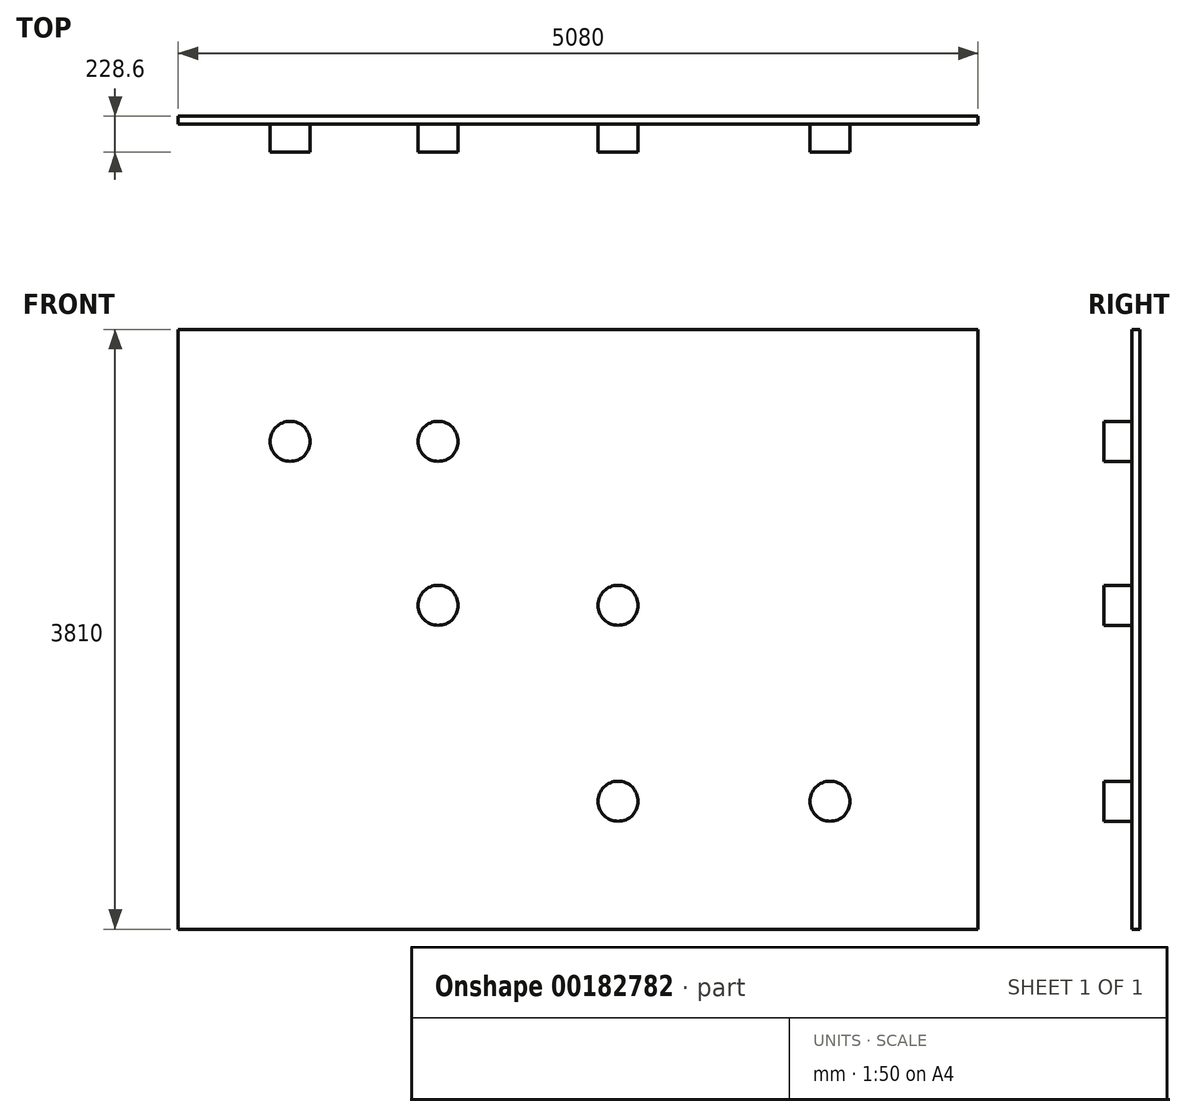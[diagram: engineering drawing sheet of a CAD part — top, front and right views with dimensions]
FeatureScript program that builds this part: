
annotation { "Feature Type Name" : "Feature", "Feature Type Description" : "" }
export const myFeature = defineFeature(function(context is Context, id is Id, definition is map)
    precondition{}
    {
        {
            var Q0;
            Q0=qCreatedBy(makeId("Front.planeOp"),FACE);
            var sketch = newSketch(context, id + "F0", { "sketchPlane" : qUnion([Q0])});
            skLineSegment(sketch, "E0.bottom", {"start": v(-126.06, 3694.01) * mm, "end": v(4953.94, 3694.01) * mm});
            skLineSegment(sketch, "E0.top", {"start": v(-126.06, -115.99) * mm, "end": v(4953.94, -115.99) * mm});
            skLineSegment(sketch, "E0.left", {"start": v(-126.06, 3694.01) * mm, "end": v(-126.06, -115.99) * mm});
            skLineSegment(sketch, "E0.right", {"start": v(4953.94, 3694.01) * mm, "end": v(4953.94, -115.99) * mm});
            skSolve(sketch);
        }
        {
            var Q0;
            Q0=makeQuery(id+"F0.imprint","IMPRINT",FACE,{"disambiguationData":[TD([[makeQuery(id+"F0.imprint","IMPRINT",EDGE,{"derivedFrom":sQuery(id+"F0.wireOp",EDGE,"E0.bottom")}),-1.0]])]});
            extrude(context, id + "F1", {"entities" : qUnion([Q0]), "depth" : 50.8 * mm});
        }
        {
            var Q0;
            Q0=makeQuery(id+"F1.opExtrude","CAP_FACE",FACE,{"disambiguationData":[OSD([sQuery(id+"F0.wireOp",EDGE,"E0.bottom"),sQuery(id+"F0.wireOp",EDGE,"E0.top"),sQuery(id+"F0.wireOp",EDGE,"E0.left"),sQuery(id+"F0.wireOp",EDGE,"E0.right")])],"isStart":false});
            var sketch = newSketch(context, id + "F2", { "sketchPlane" : qUnion([Q0])});
            skCircle(sketch, "E1", {"center": v(585.14, 2982.81) * mm, "radius": 127 * mm});
            skCircle(sketch, "E2", {"center": v(1524.94, 2982.81) * mm, "radius": 127 * mm});
            skCircle(sketch, "E3", {"center": v(1524.94, 1941.41) * mm, "radius": 127 * mm});
            skCircle(sketch, "E4", {"center": v(2667.94, 1941.41) * mm, "radius": 127 * mm});
            skCircle(sketch, "E5", {"center": v(2667.94, 696.81) * mm, "radius": 127 * mm});
            skCircle(sketch, "E6", {"center": v(4014.14, 696.81) * mm, "radius": 127 * mm});
            skSolve(sketch);
        }
        {
            var Q0;
            Q0 = qSketchRegion(id + "F2", true);
            extrude(context, id + "F3", {"entities" : qUnion([Q0]), "operationType" : NewBodyOperationType.ADD, "depth" : 177.8 * mm});
        }
    });
